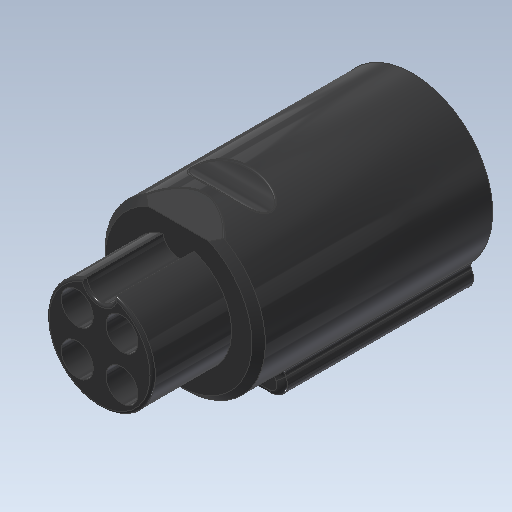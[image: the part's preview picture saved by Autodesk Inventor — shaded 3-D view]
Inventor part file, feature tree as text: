
AUTODESK INVENTOR PART (.ipt)
format: ipt  version: 2020 (Build 240168000, 168)  size: 414,208 bytes
history: native  units: in
note: dims shown in document units (in); Inventor stores cm internally (conversion verified against a paired STEP export)
features: extrude x10, sketch x10, fillet x6, chamfer x1, projected_geometry x1
ambient origin geometry x7: Origin, XZ Plane, XY Plane, X Axis, Y Axis, Z Axis, Center Point
bodies: Solid1 (feature_tree)
feature tree (28):
  extrude  "ExtrusionBlind1"  TaperAngle=0.0deg  [1 undecoded]
  extrude  "ExtrusionMidThru1"  Depth=0.005in
  chamfer  "Chamfer2"  Distance=0.1in
  extrude  "ExtrusionBlind2"  Depth=0.004in
  fillet  "Fillet15"  Radius=0.059in
  fillet  "Fillet16"  Radius=0.13in
  extrude  "Extrusion14"  Depth=0.087in TaperAngle=0.0deg
  extrude  "ExtrusionBlind9"  Depth=0.031in TaperAngle=0.0deg
  extrude  "ExtrusionThru1"  Depth=0.13in TaperAngle=0.0deg
  extrude  "ExtrusionBlind10"  Depth=0.003in
  extrude  "ExtrusionBlind11"  Depth=0.003in
  extrude  "ExtrusionThru2"  Depth=0.002in
  extrude  "ExtrusionBlind12"  Depth=0.002in TaperAngle=0.0deg
  fillet  "Fillet17"  Radius=0.12in
  fillet  "Fillet18"  Radius=0.015in
  fillet  "Fillet19"  Radius=0.1855in
  fillet  "Fillet20"  Radius=0.042in
  sketch  "Sketch4-<F>"  dims[d22=0.132in d23=0.0in d28=0.0in]
  sketch  "Sketch5-<F>"  dims[d29=0.13in d30=0.0in d31=0.005in d32=0.005in]
  sketch  "Sketch6-<F>"  dims[d33=45.0deg]
  sketch  "Sketch8-<U>"  dims[d34=0.002in d35=0.1in d36=0.0in]
  sketch  "Sketch9-<F>"  dims[d37=0.004in d38=0.004in d41=0.059in d42=0.0in d43=0.13in d44=0.0in]
  sketch  "Sketch10-<F>"  dims[d45=0.0in d46=0.087in d47=0.0in]
  sketch  "Sketch11-<F>"  dims[d48=0.0in d49=0.031in d50=0.0in]
  sketch  "Sketch12-<F>"  dims[d51=0.0in d52=0.13in d53=0.0in]
  sketch  "Sketch13-<F>"  dims[d54=0.035in d55=0.0in d56=0.003in]
  sketch  "Sketch15-<F>"  dims[d57=0.004in d58=0.003in d59=0.002in d65=0.043in d66=0.0in d78=0.12in d79=0.015in d80=0.1855in d81=0.042in d82=0.0185in d85=0.04in d86=0.0075in d87=0.0095in d88=0.0725in d89=0.0046in d90=0.0046in d92=0.0405in d93=0.0235in d94=0.0334in d95=0.0334in d96=0.024in d98=0.022in d99=0.039in d100=0.008in d101=0.008in d102=0.085in]
  projected_geometry  "Projected Loop1"
note: 1 required parameter value undecoded (feature->parameter linkage not recoverable at this tier; creation-order binding heuristic only, values carry confidence <= 0.55)
